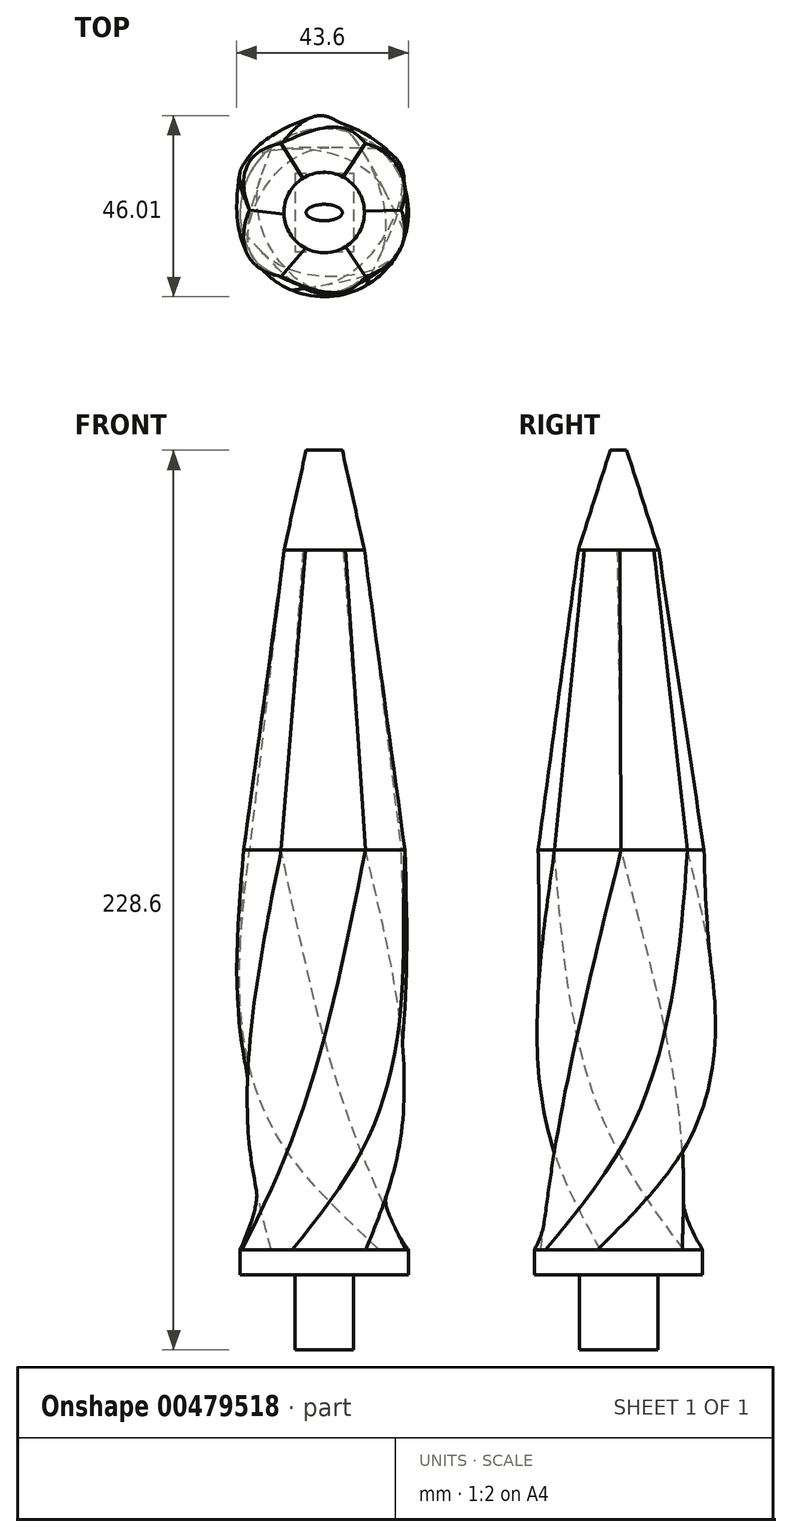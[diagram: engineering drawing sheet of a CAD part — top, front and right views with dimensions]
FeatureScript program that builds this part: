
annotation { "Feature Type Name" : "Feature", "Feature Type Description" : "" }
export const myFeature = defineFeature(function(context is Context, id is Id, definition is map)
    precondition{}
    {
        {
            var Q0;
            Q0=qCreatedBy(makeId("Top.planeOp"),FACE);
            cPlane(context, id + "F0", {"entities" : qUnion([Q0]), "cplaneType" : CPlaneType.OFFSET, "offset" : 25.4 * mm, "width" : 152.4 * mm, "height" : 152.4 * mm});
        }
        {
            var Q0;
            Q0=qCreatedBy(makeId("Top.planeOp"),FACE);
            var sketch = newSketch(context, id + "F1", { "sketchPlane" : qUnion([Q0])});
            skArc(sketch, "E0", {"start": v(-13.45, 16.62) * mm, "mid": v(-20.16, 7.11) * mm, "end": v(-20.9, -4.5) * mm});
            skArc(sketch, "E1", {"start": v(14, 16.17) * mm, "mid": v(0.35, 21.38) * mm, "end": v(-13.45, 16.62) * mm});
            skArc(sketch, "E2", {"start": v(-20.9, -4.5) * mm, "mid": v(-16.41, -13.7) * mm, "end": v(-8.17, -19.76) * mm});
            skArc(sketch, "E3", {"start": v(20.69, -5.4) * mm, "mid": v(20.42, 6.34) * mm, "end": v(14, 16.17) * mm});
            skArc(sketch, "E4", {"start": v(-8.17, -19.76) * mm, "mid": v(1.32, -21.34) * mm, "end": v(10.55, -18.6) * mm});
            skArc(sketch, "E5", {"start": v(10.55, -18.6) * mm, "mid": v(16.96, -13.02) * mm, "end": v(20.69, -5.4) * mm});
            skSolve(sketch);
        }
        {
            var Q0;
            Q0=qCreatedBy(id+"F0.planeOp",FACE);
            var sketch = newSketch(context, id + "F2", { "sketchPlane" : qUnion([Q0])});
            skCircle(sketch, "E6.cCircle", {"center": v(0, 0) * mm, "radius": 16.36 * mm, "construction": true});
            skLineSegment(sketch, "E6.0", {"start": v(-9.2, -16.5) * mm, "end": v(-18.89, -0.27) * mm});
            skLineSegment(sketch, "E6.1", {"start": v(-18.89, -0.27) * mm, "end": v(-9.68, 16.22) * mm});
            skLineSegment(sketch, "E6.2", {"start": v(-9.68, 16.22) * mm, "end": v(9.2, 16.5) * mm});
            skLineSegment(sketch, "E6.3", {"start": v(9.2, 16.5) * mm, "end": v(18.89, 0.27) * mm});
            skLineSegment(sketch, "E6.4", {"start": v(18.89, 0.27) * mm, "end": v(9.68, -16.22) * mm});
            skLineSegment(sketch, "E6.5", {"start": v(9.68, -16.22) * mm, "end": v(-9.2, -16.5) * mm});
            skPoint(sketch, "E6.0.midPoint", {"position": v(-14.05, -8.38) * mm});
            skSolve(sketch);
        }
        {
            var Q0;
            Q0=qCreatedBy(makeId("Top.planeOp"),FACE);
            cPlane(context, id + "F3", {"entities" : qUnion([Q0]), "cplaneType" : CPlaneType.OFFSET, "offset" : 25.4 * mm, "oppositeDirection" : true, "width" : 152.4 * mm, "height" : 152.4 * mm});
        }
        {
            var Q0;
            Q0=qCreatedBy(id+"F3.planeOp",FACE);
            var sketch = newSketch(context, id + "F4", { "sketchPlane" : qUnion([Q0])});
            skLineSegment(sketch, "E7.bottom", {"start": v(-7.48, 9.97) * mm, "end": v(7.48, 9.97) * mm});
            skLineSegment(sketch, "E7.top", {"start": v(-7.48, -9.97) * mm, "end": v(7.48, -9.97) * mm});
            skLineSegment(sketch, "E7.left", {"start": v(-7.48, 9.97) * mm, "end": v(-7.48, -9.97) * mm});
            skLineSegment(sketch, "E7.right", {"start": v(7.48, 9.97) * mm, "end": v(7.48, -9.97) * mm});
            skPoint(sketch, "E7.middle", {"position": v(0, 0) * mm});
            skSolve(sketch);
        }
        {
            var Q0;
            Q0=makeQuery(id+"F4.imprint","IMPRINT",FACE,{"disambiguationData":[TD([[makeQuery(id+"F4.imprint","IMPRINT",EDGE,{"derivedFrom":sQuery(id+"F4.wireOp",EDGE,"E7.bottom")}),-1.0]])]});
            extrude(context, id + "F5", {"entities" : qUnion([Q0]), "depth" : 25.4 * mm});
        }
        {
            var Q0;
            Q0=makeQuery(id+"F1.imprint","IMPRINT",FACE,{"disambiguationData":[TD([[makeQuery(id+"F1.imprint","IMPRINT",EDGE,{"derivedFrom":sQuery(id+"F1.wireOp",EDGE,"E0")}),1.0]])]});
            extrude(context, id + "F6", {"entities" : qUnion([Q0]), "operationType" : NewBodyOperationType.ADD, "oppositeDirection" : true, "depth" : 6.35 * mm});
        }
        {
            var Q0;
            Q0=qCreatedBy(id+"F0.planeOp",FACE);
            cPlane(context, id + "F7", {"entities" : qUnion([Q0]), "cplaneType" : CPlaneType.OFFSET, "offset" : 76.2 * mm, "width" : 152.4 * mm, "height" : 152.4 * mm});
        }
        {
            var Q0;
            Q0=qCreatedBy(id+"F7.planeOp",FACE);
            var sketch = newSketch(context, id + "F8", { "sketchPlane" : qUnion([Q0])});
            skFitSpline(sketch, "E8", {"points": [v(19.53, 0.67) * mm, v(10.47, 17.57) * mm], "startDerivative": vector(10.88, 27.87) * mm, "endDerivative": vector(-16.31, 4.08) * mm});
            skFitSpline(sketch, "E9", {"points": [v(10.47, 17.57) * mm, v(-10.93, 17.57) * mm], "startDerivative": vector(-13.6, 17.67) * mm, "endDerivative": vector(-32.93, -15.7) * mm});
            skFitSpline(sketch, "E10", {"points": [v(-10.93, 17.57) * mm, v(-18.99, 0.67) * mm], "startDerivative": vector(-18.28, -2.66) * mm, "endDerivative": vector(13.6, -33.3) * mm});
            skLineSegment(sketch, "E11", {"start": v(19.53, 0.67) * mm, "end": v(-18.99, 0.67) * mm, "construction": true});
            skFitSpline(sketch, "E12.MirrorCS", {"points": [v(-10.93, -16.23) * mm, v(-18.99, 0.67) * mm], "startDerivative": vector(-18.28, 2.66) * mm, "endDerivative": vector(13.6, 33.3) * mm});
            skFitSpline(sketch, "E13.MirrorCS", {"points": [v(10.47, -16.23) * mm, v(-10.93, -16.23) * mm], "startDerivative": vector(-13.6, -17.67) * mm, "endDerivative": vector(-32.93, 15.7) * mm});
            skFitSpline(sketch, "E14.MirrorCS", {"points": [v(19.53, 0.67) * mm, v(10.47, -16.23) * mm], "startDerivative": vector(10.88, -27.87) * mm, "endDerivative": vector(-16.31, -4.08) * mm});
            skSolve(sketch);
        }
        {
            var Q1;
            Q1 = qSketchRegion(id + "F1", true);
            var Q2;
            Q2 = qSketchRegion(id + "F2", true);
            var Q3;
            Q3=makeQuery(id+"F8.imprint","IMPRINT",FACE,{"disambiguationData":[TD([[makeQuery(id+"F8.imprint","IMPRINT",EDGE,{"derivedFrom":sQuery(id+"F8.wireOp",EDGE,"E8")}),1.0]])]});
            var Q4;
            Q4=sQuery(id+"F1.wireOp",VERTEX,"E5.start");
            var Q5;
            Q5=sQuery(id+"F2.wireOp",VERTEX,"E6.4.start");
            var Q6;
            Q6=sQuery(id+"F8.wireOp",VERTEX,"E9.0.internal");
            loft(context, id + "F9", {"operationType" : NewBodyOperationType.ADD, "sheetProfilesArray" : [{ "sheetProfileEntities" : qUnion([Q1]) }, { "sheetProfileEntities" : qUnion([Q2]) }, { "sheetProfileEntities" : qUnion([Q3]) }], "matchConnections" : true, "connections" : [{ "connectionEntities" : qUnion([Q4, Q5, Q6]), "connectionEdgeQueries" : qUnion([]), "connectionEdgeParameters" : [] }]});
        }
        {
            var Q0;
            Q0=qCreatedBy(id+"F7.planeOp",FACE);
            cPlane(context, id + "F10", {"entities" : qUnion([Q0]), "cplaneType" : CPlaneType.OFFSET, "offset" : 76.2 * mm, "width" : 152.4 * mm, "height" : 152.4 * mm});
        }
        {
            var Q0;
            Q0=qCreatedBy(id+"F10.planeOp",FACE);
            var sketch = newSketch(context, id + "F11", { "sketchPlane" : qUnion([Q0])});
            skCircle(sketch, "E15", {"center": v(0, 0) * mm, "radius": 10.22 * mm});
            skSolve(sketch);
        }
        {
            var Q1;
            Q1=makeQuery(id+"F11.imprint","IMPRINT",FACE,{"disambiguationData":[TD([[makeQuery(id+"F11.imprint","IMPRINT",EDGE,{"derivedFrom":sQuery(id+"F11.wireOp",EDGE,"E15")}),1.0]])]});
            var Q2;
            Q2=makeQuery(id+"F8.imprint","IMPRINT",FACE,{"disambiguationData":[TD([[makeQuery(id+"F8.imprint","IMPRINT",EDGE,{"derivedFrom":sQuery(id+"F8.wireOp",EDGE,"E8")}),1.0]])]});
            loft(context, id + "F12", {"operationType" : NewBodyOperationType.ADD, "sheetProfilesArray" : [{ "sheetProfileEntities" : qUnion([Q1]) }, { "sheetProfileEntities" : qUnion([Q2]) }]});
        }
        {
            var Q0;
            Q0=qCreatedBy(id+"F10.planeOp",FACE);
            cPlane(context, id + "F13", {"entities" : qUnion([Q0]), "cplaneType" : CPlaneType.OFFSET, "offset" : 25.4 * mm, "width" : 152.4 * mm, "height" : 152.4 * mm});
        }
        {
            var Q0;
            Q0=qCreatedBy(id+"F13.planeOp",FACE);
            var sketch = newSketch(context, id + "F14", { "sketchPlane" : qUnion([Q0])});
            skEllipse(sketch, "E16", {"center": v(0, 0) * mm, "majorRadius": 4.6 * mm, "minorRadius": 2.08 * mm, "majorAxis": v(1, 0)});
            skSolve(sketch);
        }
        {
            var Q1;
            Q1=makeQuery(id+"F12.opLoft","CAP_FACE",FACE,{"disambiguationData":[OSD([makeQuery(id+"F11.imprint","IMPRINT",FACE,{"disambiguationData":[TD([[makeQuery(id+"F11.imprint","IMPRINT",EDGE,{"derivedFrom":sQuery(id+"F11.wireOp",EDGE,"E15")}),1.0]])]})])],"isStart":true});
            var Q2;
            Q2 = qSketchRegion(id + "F14", true);
            loft(context, id + "F15", {"operationType" : NewBodyOperationType.ADD, "sheetProfilesArray" : [{ "sheetProfileEntities" : qUnion([Q1]) }, { "sheetProfileEntities" : qUnion([Q2]) }]});
        }
    });
